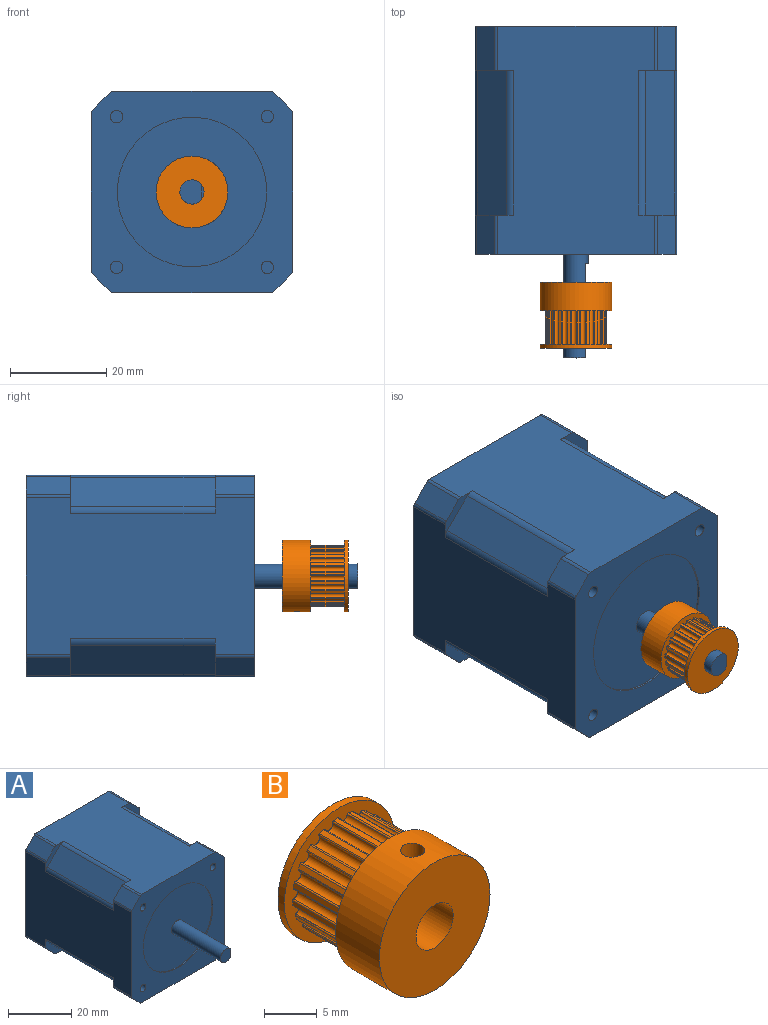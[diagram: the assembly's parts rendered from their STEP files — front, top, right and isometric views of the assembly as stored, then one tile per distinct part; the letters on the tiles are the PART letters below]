
ASSEMBLY  parts=2 mates=1
PART A: 78 faces, bbox 41.8x68.8x41.8 mm
  f0: plane 41.84x41.84mm, normal (0,-1,0), area 938.4mm2, adj f1,f2,f3,f4,f10,f17,f19,f21
  f1: plane 47.3x32.53mm, normal (-1,0,0), area 1343.9mm2, adj f0,f5,f6,f7,f43,f44,f45,f50
  f2: plane 47.3x32.53mm, normal (1,0,0), area 1331.4mm2, adj f0,f5,f33,f36,f37,f40,f41,f48
  f3: plane 47.3x32.53mm, normal (0,0,1), area 1343.9mm2, adj f0,f5,f6,f7,f36,f37,f49,f52
  f4: plane 47.3x32.53mm, normal (0,0,-1), area 1343.9mm2, adj f0,f5,f40,f41,f43,f44,f46,f47
  f5: plane 41.84x41.84mm, normal (0,1,0), area 1545.4mm2, adj f1,f2,f3,f4,f12,f25,f27,f29
  f6: plane 7.9x7.9mm, normal (0,1,0), area 16.1mm2, adj f1,f3,f38,f49,f50,f58,f63,f64
  f7: plane 7.9x7.9mm, normal (0,-1,0), area 16.1mm2, adj f1,f3,f38,f49,f50,f57,f75,f76
  f8: cylinder r=2.5mm len=21.9mm, axis (0,-1,0), area 282.6mm2, adj f9,f11,f14,f77
  f9: plane 19.5x2.95mm, normal (1,0,0), area 57.4mm2, adj f8,f14,f77
  f10: cylinder r=15.5mm len=31mm, axis (0,-1,0), area 39mm2, adj f0,f11
  f11: plane 31x31mm, normal (0,-1,0), area 735.1mm2, adj f8,f10
  f12: cylinder r=4.22mm len=8.44mm, axis (0,1,0), area 70.5mm2, adj f5,f13
  f13: plane 8.44x8.44mm, normal (0,1,0), area 36.3mm2, adj f12,f15
  f14: plane 2.95x0.48mm, normal (0,-1,0), area 1mm2, adj f8,f9
  f15: cylinder r=2.5mm len=5mm, axis (0,1,0), area 13.5mm2, adj f13,f16
  f16: plane 5x5mm, normal (0,1,0), area 19.6mm2, adj f15
  f17: cylinder r=1.3mm len=8mm, axis (0,-1,0), area 65.3mm2, adj f0,f18
  f18: plane 2.6x2.6mm, normal (0,-1,0), area 5.3mm2, adj f17
  f19: cylinder r=1.3mm len=8mm, axis (0,-1,0), area 65.3mm2, adj f0,f20
  f20: plane 2.6x2.6mm, normal (0,-1,0), area 5.3mm2, adj f19
  f21: cylinder r=1.3mm len=8mm, axis (0,-1,0), area 65.3mm2, adj f0,f22
  f22: plane 2.6x2.6mm, normal (0,-1,0), area 5.3mm2, adj f21
  f23: cylinder r=1.3mm len=8mm, axis (0,-1,0), area 65.3mm2, adj f0,f24
  f24: plane 2.6x2.6mm, normal (0,-1,0), area 5.3mm2, adj f23
  f25: cylinder r=3mm len=6mm, axis (0,1,0), area 18.8mm2, adj f5,f26
  f26: plane 6x6mm, normal (0,1,0), area 28.3mm2, adj f25
  f27: cylinder r=3mm len=6mm, axis (0,1,0), area 18.8mm2, adj f5,f28
  f28: plane 6x6mm, normal (0,1,0), area 28.3mm2, adj f27
  f29: cylinder r=3mm len=6mm, axis (0,1,0), area 18.8mm2, adj f5,f30
  f30: plane 6x6mm, normal (0,1,0), area 28.3mm2, adj f29
  f31: cylinder r=3mm len=6mm, axis (0,1,0), area 18.8mm2, adj f5,f32
  f32: plane 6x6mm, normal (0,1,0), area 28.3mm2, adj f31
  f33: cylinder r=2mm len=4mm, axis (1,0,0), area 37.7mm2, adj f2,f34
  f34: plane 4x4mm, normal (1,0,0), area 12.6mm2, adj f33
  f35: plane 30x5.9mm, normal (0.71,0,0.71), area 250.3mm2, adj f36,f37,f51,f52
  f36: plane 7.9x7.9mm, normal (0,1,0), area 16.1mm2, adj f2,f3,f35,f51,f52,f60,f61,f62
  f37: plane 7.9x7.9mm, normal (0,-1,0), area 16.1mm2, adj f2,f3,f35,f51,f52,f59,f71,f72
  f38: plane 30x5.9mm, normal (-0.71,0,0.71), area 250.3mm2, adj f6,f7,f49,f50
  f39: plane 30x5.9mm, normal (0.71,0,-0.71), area 250.3mm2, adj f40,f41,f47,f48
  f40: plane 7.9x7.9mm, normal (0,1,0), area 16.1mm2, adj f2,f4,f39,f47,f48,f56,f65,f66
  f41: plane 7.9x7.9mm, normal (0,-1,0), area 16.1mm2, adj f2,f4,f39,f47,f48,f55,f69,f70
  f42: plane 30x5.9mm, normal (-0.71,0,-0.71), area 250.3mm2, adj f43,f44,f45,f46
  f43: plane 7.9x7.9mm, normal (0,1,0), area 16.1mm2, adj f1,f4,f42,f45,f46,f54,f67,f68
  f44: plane 7.9x7.9mm, normal (0,-1,0), area 16.1mm2, adj f1,f4,f42,f45,f46,f53,f73,f74
  f45: cylinder r=2mm len=30mm, axis (0,-1,0), area 47.1mm2, adj f1,f42,f43,f44
  f46: cylinder r=2mm len=30mm, axis (0,-1,0), area 47.1mm2, adj f4,f42,f43,f44
  f47: cylinder r=2mm len=30mm, axis (0,-1,0), area 47.1mm2, adj f4,f39,f40,f41
  f48: cylinder r=2mm len=30mm, axis (0,1,0), area 47.1mm2, adj f2,f39,f40,f41
  f49: cylinder r=2mm len=30mm, axis (0,-1,0), area 47.1mm2, adj f3,f6,f7,f38
  f50: cylinder r=2mm len=30mm, axis (0,1,0), area 47.1mm2, adj f1,f6,f7,f38
  f51: cylinder r=2mm len=30mm, axis (0,1,0), area 47.1mm2, adj f2,f35,f36,f37
  f52: cylinder r=2mm len=30mm, axis (0,1,0), area 47.1mm2, adj f3,f35,f36,f37
  f53: plane 9.2x3.66mm, normal (-0.71,0,-0.71), area 47.6mm2, adj f5,f44,f73,f74
  f54: plane 8.1x3.66mm, normal (-0.71,0,-0.71), area 41.9mm2, adj f0,f43,f67,f68
  f55: plane 9.2x3.66mm, normal (0.71,0,-0.71), area 47.6mm2, adj f5,f41,f69,f70
  f56: plane 8.1x3.66mm, normal (0.71,0,-0.71), area 41.9mm2, adj f0,f40,f65,f66
  f57: plane 9.2x3.66mm, normal (-0.71,0,0.71), area 47.6mm2, adj f5,f7,f75,f76
  f58: plane 8.1x3.66mm, normal (-0.71,0,0.71), area 41.9mm2, adj f0,f6,f63,f64
  f59: plane 9.2x3.66mm, normal (0.71,0,0.71), area 47.6mm2, adj f5,f37,f71,f72
  f60: plane 8.1x3.66mm, normal (0.71,0,0.71), area 41.9mm2, adj f0,f36,f61,f62
  f61: cylinder r=1mm len=8.1mm, axis (0,1,0), area 6.4mm2, adj f0,f2,f36,f60
  f62: cylinder r=1mm len=8.1mm, axis (0,1,0), area 6.4mm2, adj f0,f3,f36,f60
  f63: cylinder r=1mm len=8.1mm, axis (0,-1,0), area 6.4mm2, adj f0,f3,f6,f58
  f64: cylinder r=1mm len=8.1mm, axis (0,1,0), area 6.4mm2, adj f0,f1,f6,f58
  f65: cylinder r=1mm len=8.1mm, axis (0,-1,0), area 6.4mm2, adj f0,f4,f40,f56
  f66: cylinder r=1mm len=8.1mm, axis (0,1,0), area 6.4mm2, adj f0,f2,f40,f56
  f67: cylinder r=1mm len=8.1mm, axis (0,-1,0), area 6.4mm2, adj f0,f1,f43,f54
  f68: cylinder r=1mm len=8.1mm, axis (0,-1,0), area 6.4mm2, adj f0,f4,f43,f54
  f69: cylinder r=1mm len=9.2mm, axis (0,-1,0), area 7.2mm2, adj f4,f5,f41,f55
  f70: cylinder r=1mm len=9.2mm, axis (0,1,0), area 7.2mm2, adj f2,f5,f41,f55
  f71: cylinder r=1mm len=9.2mm, axis (0,1,0), area 7.2mm2, adj f2,f5,f37,f59
  f72: cylinder r=1mm len=9.2mm, axis (0,1,0), area 7.2mm2, adj f3,f5,f37,f59
  f73: cylinder r=1mm len=9.2mm, axis (0,-1,0), area 7.2mm2, adj f4,f5,f44,f53
  f74: cylinder r=1mm len=9.2mm, axis (0,-1,0), area 7.2mm2, adj f1,f5,f44,f53
  f75: cylinder r=1mm len=9.2mm, axis (0,1,0), area 7.2mm2, adj f1,f5,f7,f57
  f76: cylinder r=1mm len=9.2mm, axis (0,-1,0), area 7.2mm2, adj f3,f5,f7,f57
  f77: plane 5x4.52mm, normal (0,-1,0), area 18.7mm2, adj f8,f9
PART B: 128 faces, bbox 14.9x13.7x14.9 mm
  f0: cylinder r=2.5mm len=13.65mm, axis (0,-1,0), area 210.1mm2, adj f122,f125,f127
  f1: cylinder r=7.45mm len=14.9mm, axis (0,1,0), area 272mm2, adj f122,f123,f127
  f2: cylinder r=0.14mm len=6.9mm, axis (0,-1,0), area 1.6mm2, adj f3,f121,f123,f126
  f3: plane 6.9x0.01mm, normal (0.15,0,-0.99), area 0.1mm2, adj f2,f4,f123,f126
  f4: cylinder r=0.55mm len=6.9mm, axis (0,-1,0), area 11.6mm2, adj f3,f5,f123,f126
  f5: plane 6.9x0.01mm, normal (-0.32,0,0.95), area 0.1mm2, adj f4,f6,f123,f126
  f6: cylinder r=0.14mm len=6.9mm, axis (0,-1,0), area 1.6mm2, adj f5,f7,f123,f126
  f7: plane 6.9x0.53mm, normal (-0.92,0,-0.39), area 3.9mm2, adj f6,f8,f123,f126
  f8: cylinder r=0.14mm len=6.9mm, axis (0,-1,0), area 1.6mm2, adj f7,f9,f123,f126
  f9: plane 6.9x0.01mm, normal (0.45,0,-0.89), area 0.1mm2, adj f8,f10,f123,f126
  f10: cylinder r=0.55mm len=6.9mm, axis (0,-1,0), area 11.6mm2, adj f9,f11,f123,f126
  f11: plane 6.9x0.01mm, normal (-0.6,0,0.8), area 0.1mm2, adj f10,f12,f123,f126
  f12: cylinder r=0.14mm len=6.9mm, axis (0,-1,0), area 1.6mm2, adj f11,f13,f123,f126
  f13: plane 6.9x0.43mm, normal (-0.76,0,-0.65), area 3.9mm2, adj f12,f14,f123,f126
  f14: cylinder r=0.14mm len=6.9mm, axis (0,-1,0), area 1.6mm2, adj f13,f15,f123,f126
  f15: plane 6.9x0.01mm, normal (0.7,0,-0.71), area 0.1mm2, adj f14,f16,f123,f126
  f16: cylinder r=0.55mm len=6.9mm, axis (0,-1,0), area 11.6mm2, adj f15,f17,f123,f126
  f17: plane 6.9x0.01mm, normal (-0.82,0,0.58), area 0.1mm2, adj f16,f18,f123,f126
  f18: cylinder r=0.14mm len=6.9mm, axis (0,-1,0), area 1.6mm2, adj f17,f19,f123,f126
  f19: plane 6.9x0.49mm, normal (-0.52,0,-0.85), area 3.9mm2, adj f18,f20,f123,f126
  f20: cylinder r=0.14mm len=6.9mm, axis (0,-1,0), area 1.6mm2, adj f19,f21,f123,f126
  f21: plane 6.9x0.01mm, normal (0.89,0,-0.46), area 0.1mm2, adj f20,f22,f123,f126
  f22: cylinder r=0.55mm len=6.9mm, axis (0,-1,0), area 11.6mm2, adj f21,f23,f123,f126
  f23: plane 6.9x0.01mm, normal (-0.95,0,0.3), area 0.1mm2, adj f22,f24,f123,f126
  f24: cylinder r=0.14mm len=6.9mm, axis (0,-1,0), area 1.6mm2, adj f23,f25,f123,f126
  f25: plane 6.9x0.56mm, normal (-0.23,0,-0.97), area 3.9mm2, adj f24,f26,f123,f126
  f26: cylinder r=0.14mm len=6.9mm, axis (0,-1,0), area 1.6mm2, adj f25,f27,f123,f126
  f27: plane 6.9x0.01mm, normal (0.99,0,-0.16), area 0.1mm2, adj f26,f28,f123,f126
  f28: cylinder r=0.55mm len=6.9mm, axis (0,-1,0), area 11.6mm2, adj f27,f29,f123,f126
  f29: plane 6.9x0.01mm, normal (-1,0,-0.01), area 0.1mm2, adj f28,f30,f123,f126
  f30: cylinder r=0.14mm len=6.9mm, axis (0,-1,0), area 1.6mm2, adj f29,f31,f123,f126
  f31: plane 6.9x0.57mm, normal (0.08,0,-1), area 3.9mm2, adj f30,f32,f123,f126
  f32: cylinder r=0.14mm len=6.9mm, axis (0,-1,0), area 1.6mm2, adj f31,f33,f123,f126
  f33: plane 6.9x0.01mm, normal (0.99,0,0.15), area 0.1mm2, adj f32,f34,f123,f126
  f34: cylinder r=0.55mm len=6.9mm, axis (0,-1,0), area 11.6mm2, adj f33,f35,f123,f126
  f35: plane 6.9x0.01mm, normal (-0.95,0,-0.32), area 0.1mm2, adj f34,f36,f123,f126
  f36: cylinder r=0.14mm len=6.9mm, axis (0,-1,0), area 1.6mm2, adj f35,f37,f123,f126
  f37: plane 6.9x0.53mm, normal (0.39,0,-0.92), area 3.9mm2, adj f36,f38,f123,f126
  f38: cylinder r=0.14mm len=6.9mm, axis (0,-1,0), area 1.6mm2, adj f37,f39,f123,f126
  f39: plane 6.9x0.01mm, normal (0.89,0,0.45), area 0.1mm2, adj f38,f40,f123,f126
  f40: cylinder r=0.55mm len=6.9mm, axis (0,-1,0), area 11.6mm2, adj f39,f41,f123,f126
  f41: plane 6.9x0.01mm, normal (-0.8,0,-0.6), area 0.1mm2, adj f40,f42,f123,f126
  f42: cylinder r=0.14mm len=6.9mm, axis (0,-1,0), area 1.6mm2, adj f41,f43,f123,f126
  f43: plane 6.9x0.43mm, normal (0.65,0,-0.76), area 3.9mm2, adj f42,f44,f123,f126
  f44: cylinder r=0.14mm len=6.9mm, axis (0,-1,0), area 1.6mm2, adj f43,f45,f123,f126
  f45: plane 6.9x0.01mm, normal (0.71,0,0.7), area 0.1mm2, adj f44,f46,f123,f126
  f46: cylinder r=0.55mm len=6.9mm, axis (0,-1,0), area 11.6mm2, adj f45,f47,f123,f126
  f47: plane 6.9x0.01mm, normal (-0.58,0,-0.82), area 0.1mm2, adj f46,f48,f123,f126
  f48: cylinder r=0.14mm len=6.9mm, axis (0,-1,0), area 1.6mm2, adj f47,f49,f123,f126
  f49: plane 6.9x0.49mm, normal (0.85,0,-0.52), area 3.9mm2, adj f48,f50,f123,f126
  f50: cylinder r=0.14mm len=6.9mm, axis (0,-1,0), area 1.6mm2, adj f49,f51,f123,f126
  f51: plane 6.9x0.01mm, normal (0.46,0,0.89), area 0.1mm2, adj f50,f52,f123,f126
  f52: cylinder r=0.55mm len=6.9mm, axis (0,-1,0), area 11.6mm2, adj f51,f53,f123,f126
  f53: plane 6.9x0.01mm, normal (-0.3,0,-0.95), area 0.1mm2, adj f52,f54,f123,f126
  f54: cylinder r=0.14mm len=6.9mm, axis (0,-1,0), area 1.6mm2, adj f53,f55,f123,f126
  f55: plane 6.9x0.56mm, normal (0.97,0,-0.23), area 3.9mm2, adj f54,f56,f123,f126
  f56: cylinder r=0.14mm len=6.9mm, axis (0,-1,0), area 1.6mm2, adj f55,f57,f123,f126
  f57: plane 6.9x0.01mm, normal (0.16,0,0.99), area 0.1mm2, adj f56,f58,f123,f126
  f58: cylinder r=0.55mm len=6.9mm, axis (0,-1,0), area 11.6mm2, adj f57,f59,f123,f126
  f59: plane 6.9x0.01mm, normal (0.01,0,-1), area 0.1mm2, adj f58,f60,f123,f126
  f60: cylinder r=0.14mm len=6.9mm, axis (0,-1,0), area 1.6mm2, adj f59,f61,f123,f126
  f61: plane 6.9x0.57mm, normal (1,0,0.08), area 3.9mm2, adj f60,f62,f123,f126
  f62: cylinder r=0.14mm len=6.9mm, axis (0,-1,0), area 1.6mm2, adj f61,f63,f123,f126
  f63: plane 6.9x0.01mm, normal (-0.15,0,0.99), area 0.1mm2, adj f62,f64,f123,f126
  f64: cylinder r=0.55mm len=6.9mm, axis (0,-1,0), area 11.6mm2, adj f63,f65,f123,f126
  f65: plane 6.9x0.01mm, normal (0.32,0,-0.95), area 0.1mm2, adj f64,f66,f123,f126
  f66: cylinder r=0.14mm len=6.9mm, axis (0,-1,0), area 1.6mm2, adj f65,f67,f123,f126
  f67: plane 6.9x0.53mm, normal (0.92,0,0.39), area 3.9mm2, adj f66,f68,f123,f126
  f68: cylinder r=0.14mm len=6.9mm, axis (0,-1,0), area 1.6mm2, adj f67,f69,f123,f126
  f69: plane 6.9x0.01mm, normal (-0.45,0,0.89), area 0.1mm2, adj f68,f70,f123,f126
  f70: cylinder r=0.55mm len=6.9mm, axis (0,-1,0), area 11.6mm2, adj f69,f71,f123,f126
  f71: plane 6.9x0.01mm, normal (0.6,0,-0.8), area 0.1mm2, adj f70,f72,f123,f126
  f72: cylinder r=0.14mm len=6.9mm, axis (0,-1,0), area 1.6mm2, adj f71,f73,f123,f126
  f73: plane 6.9x0.43mm, normal (0.76,0,0.65), area 3.9mm2, adj f72,f74,f123,f126
  f74: cylinder r=0.14mm len=6.9mm, axis (0,-1,0), area 1.6mm2, adj f73,f75,f123,f126
  f75: plane 6.9x0.01mm, normal (-0.7,0,0.71), area 0.1mm2, adj f74,f76,f123,f126
  f76: cylinder r=0.55mm len=6.9mm, axis (0,-1,0), area 11.6mm2, adj f75,f77,f123,f126
  f77: plane 6.9x0.01mm, normal (0.82,0,-0.58), area 0.1mm2, adj f76,f78,f123,f126
  f78: cylinder r=0.14mm len=6.9mm, axis (0,-1,0), area 1.6mm2, adj f77,f79,f123,f126
  f79: plane 6.9x0.49mm, normal (0.52,0,0.85), area 3.9mm2, adj f78,f80,f123,f126
  f80: cylinder r=0.14mm len=6.9mm, axis (0,-1,0), area 1.6mm2, adj f79,f81,f123,f126
  f81: plane 6.9x0.01mm, normal (-0.89,0,0.46), area 0.1mm2, adj f80,f82,f123,f126
  f82: cylinder r=0.55mm len=6.9mm, axis (0,-1,0), area 11.6mm2, adj f81,f83,f123,f126
  f83: plane 6.9x0.01mm, normal (0.95,0,-0.3), area 0.1mm2, adj f82,f84,f123,f126
  f84: cylinder r=0.14mm len=6.9mm, axis (0,-1,0), area 1.6mm2, adj f83,f85,f123,f126
  f85: plane 6.9x0.56mm, normal (0.23,0,0.97), area 3.9mm2, adj f84,f86,f123,f126
  f86: cylinder r=0.14mm len=6.9mm, axis (0,-1,0), area 1.6mm2, adj f85,f87,f123,f126
  f87: plane 6.9x0.01mm, normal (-0.99,0,0.16), area 0.1mm2, adj f86,f88,f123,f126
  f88: cylinder r=0.55mm len=6.9mm, axis (0,-1,0), area 11.6mm2, adj f87,f89,f123,f126
  f89: plane 6.9x0.01mm, normal (1,0,0.01), area 0.1mm2, adj f88,f90,f123,f126
  f90: cylinder r=0.14mm len=6.9mm, axis (0,-1,0), area 1.6mm2, adj f89,f91,f123,f126
  f91: plane 6.9x0.57mm, normal (-0.08,0,1), area 3.9mm2, adj f90,f92,f123,f126
  f92: cylinder r=0.14mm len=6.9mm, axis (0,-1,0), area 1.6mm2, adj f91,f93,f123,f126
  f93: plane 6.9x0.01mm, normal (-0.99,0,-0.15), area 0.1mm2, adj f92,f94,f123,f126
  f94: cylinder r=0.55mm len=6.9mm, axis (0,-1,0), area 11.6mm2, adj f93,f95,f123,f126
  f95: plane 6.9x0.01mm, normal (0.95,0,0.32), area 0.1mm2, adj f94,f96,f123,f126
  f96: cylinder r=0.14mm len=6.9mm, axis (0,-1,0), area 1.6mm2, adj f95,f97,f123,f126
  f97: plane 6.9x0.53mm, normal (-0.39,0,0.92), area 3.9mm2, adj f96,f98,f123,f126
  f98: cylinder r=0.14mm len=6.9mm, axis (0,-1,0), area 1.6mm2, adj f97,f99,f123,f126
  f99: plane 6.9x0.01mm, normal (-0.89,0,-0.45), area 0.1mm2, adj f98,f100,f123,f126
  f100: cylinder r=0.55mm len=6.9mm, axis (0,-1,0), area 11.6mm2, adj f99,f101,f123,f126
  f101: plane 6.9x0.01mm, normal (0.8,0,0.6), area 0.1mm2, adj f100,f102,f123,f126
  f102: cylinder r=0.14mm len=6.9mm, axis (0,-1,0), area 1.6mm2, adj f101,f103,f123,f126
  f103: plane 6.9x0.43mm, normal (-0.65,0,0.76), area 3.9mm2, adj f102,f104,f123,f126
  f104: cylinder r=0.14mm len=6.9mm, axis (0,-1,0), area 1.6mm2, adj f103,f105,f123,f126
  f105: plane 6.9x0.01mm, normal (-0.71,0,-0.7), area 0.1mm2, adj f104,f106,f123,f126
  f106: cylinder r=0.55mm len=6.9mm, axis (0,-1,0), area 11.6mm2, adj f105,f107,f123,f126
  f107: plane 6.9x0.01mm, normal (0.58,0,0.82), area 0.1mm2, adj f106,f108,f123,f126
  f108: cylinder r=0.14mm len=6.9mm, axis (0,-1,0), area 1.6mm2, adj f107,f109,f123,f126
  f109: plane 6.9x0.49mm, normal (-0.85,0,0.52), area 3.9mm2, adj f108,f110,f123,f126
  f110: cylinder r=0.14mm len=6.9mm, axis (0,-1,0), area 1.6mm2, adj f109,f111,f123,f126
  f111: plane 6.9x0.01mm, normal (-0.46,0,-0.89), area 0.1mm2, adj f110,f112,f123,f126
  f112: cylinder r=0.55mm len=6.9mm, axis (0,-1,0), area 11.6mm2, adj f111,f113,f123,f126
  f113: plane 6.9x0.01mm, normal (0.3,0,0.95), area 0.1mm2, adj f112,f114,f123,f126
  f114: cylinder r=0.14mm len=6.9mm, axis (0,-1,0), area 1.6mm2, adj f113,f115,f123,f126
  f115: plane 6.9x0.56mm, normal (-0.97,0,0.23), area 3.9mm2, adj f114,f116,f123,f126
  f116: cylinder r=0.14mm len=6.9mm, axis (0,-1,0), area 1.6mm2, adj f115,f117,f123,f126
  f117: plane 6.9x0.01mm, normal (-0.16,0,-0.99), area 0.1mm2, adj f116,f118,f123,f126
  f118: cylinder r=0.55mm len=6.9mm, axis (0,-1,0), area 11.6mm2, adj f117,f119,f123,f126
  f119: plane 6.9x0.01mm, normal (-0.01,0,1), area 0.1mm2, adj f118,f120,f123,f126
  f120: cylinder r=0.14mm len=6.9mm, axis (0,-1,0), area 1.6mm2, adj f119,f121,f123,f126
  f121: plane 6.9x0.57mm, normal (-1,0,-0.08), area 3.9mm2, adj f2,f120,f123,f126
  f122: plane 14.9x14.9mm, normal (0,-1,0), area 154.7mm2, adj f0,f1
  f123: plane 14.9x14.9mm, normal (0,1,0), area 60.3mm2, adj f1,f2,f3,f4,f5,f6,f7,f8
  f124: cylinder r=7.45mm len=14.9mm, axis (0,-1,0), area 39.8mm2, adj f125,f126
  f125: plane 14.9x14.9mm, normal (0,1,0), area 154.7mm2, adj f0,f124
  f126: plane 14.9x14.9mm, normal (0,-1,0), area 60.3mm2, adj f2,f3,f4,f5,f6,f7,f8,f9
  f127: cylinder r=1.15mm len=5.23mm, axis (0,0,-1), area 36.4mm2, adj f0,f1
PLACE A t=(-127.19,242.61,49.05)mm
PLACE B rot(axis=(1,0,0),180deg) t=(-127.19,183.56,49.05)mm
MATE revolute B.f1 <-> A.f8  axis (0,-1,0) through (-127.19,175.81,49.05)mm
